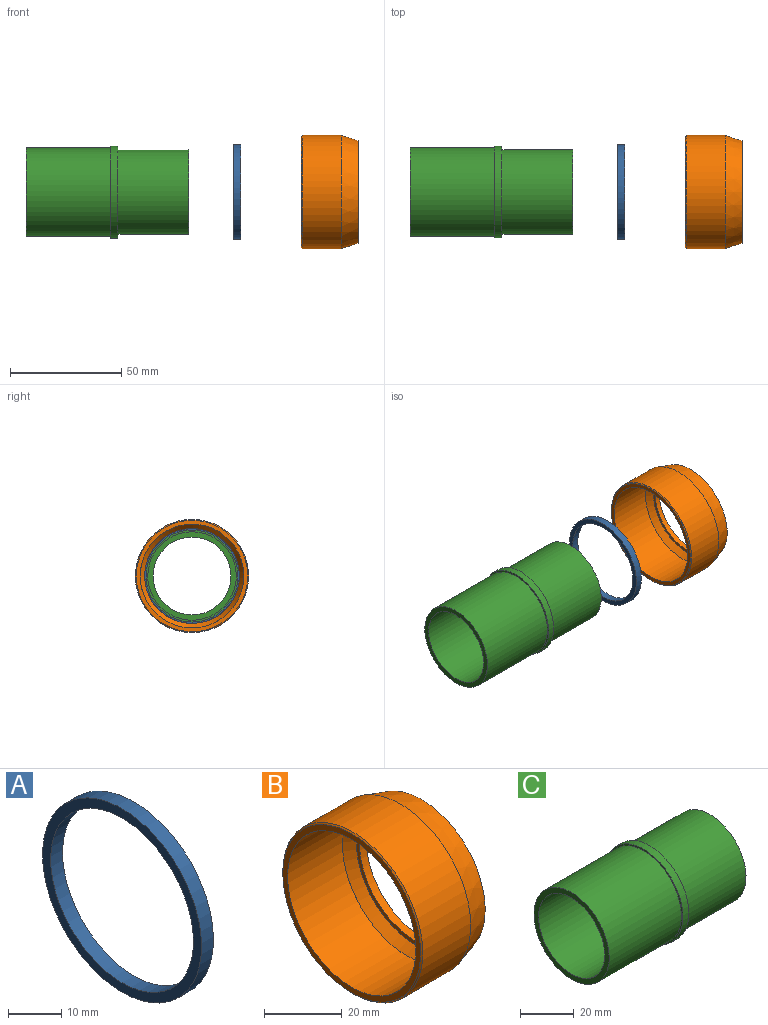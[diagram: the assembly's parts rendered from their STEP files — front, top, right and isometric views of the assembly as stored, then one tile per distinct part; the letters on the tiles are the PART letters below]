
ASSEMBLY  parts=3 mates=2
PART A: 4 faces, bbox 3.2x42.4x42.4 mm
  f0: cylinder r=19.05mm len=38.1mm, axis (-1,0,0), area 380mm2, adj f2,f3
  f1: cylinder r=21.21mm len=42.42mm, axis (-1,0,0), area 423.1mm2, adj f2,f3
  f2: plane 42.42x42.42mm, normal (1,0,0), area 273.1mm2, adj f0,f1
  f3: plane 42.42x42.42mm, normal (-1,0,0), area 273.1mm2, adj f0,f1
PART B: 11 faces, bbox 25.4x50.8x50.8 mm
  f0: cylinder r=20.12mm len=40.23mm, axis (-1,0,0), area 305mm2, adj f2,f5
  f1: cylinder r=25.4mm len=50.8mm, axis (-1,0,0), area 2774.2mm2, adj f9,f10
  f2: plane 46.08x46.08mm, normal (1,0,0), area 396mm2, adj f0,f9
  f3: plane 50.01x50.01mm, normal (-1,0,0), area 263.4mm2, adj f6,f10
  f4: cylinder r=21.27mm len=42.55mm, axis (-1,0,0), area 3.4mm2, adj f5,f8
  f5: plane 42.55x42.55mm, normal (-1,0,0), area 150.3mm2, adj f0,f4
  f6: cylinder r=23.27mm len=46.53mm, axis (-1,0,0), area 2911.1mm2, adj f3,f7
  f7: plane 46.53x46.53mm, normal (-1,0,0), area 1.9mm2, adj f6,f8
  f8: cone r=23.25mm half-angle=33deg, axis (-1,0,0), area 508.5mm2, adj f4,f7
  f9: cone r=23.04mm half-angle=17.2deg, axis (-1,0,0), area 1214mm2, adj f1,f2
  f10: cone r=25.4mm half-angle=45deg, axis (1,0,0), area 88.9mm2, adj f1,f3
PART C: 8 faces, bbox 73x41.3x41.3 mm
  f0: cylinder r=20.64mm len=41.28mm, axis (-1,0,0), area 411.7mm2, adj f4,f7
  f1: plane 38.1x38.1mm, normal (1,0,0), area 182.1mm2, adj f3,f6
  f2: plane 39.69x39.69mm, normal (-1,0,0), area 279.1mm2, adj f3,f5
  f3: cylinder r=17.46mm len=73.03mm, axis (-1,0,0), area 8012.3mm2, adj f1,f2
  f4: plane 41.28x41.28mm, normal (-1,0,0), area 100.9mm2, adj f0,f5
  f5: cylinder r=19.84mm len=39.69mm, axis (-1,0,0), area 4750.4mm2, adj f2,f4
  f6: cylinder r=19.05mm len=38.1mm, axis (1,0,0), area 3800.3mm2, adj f1,f7
  f7: plane 41.28x41.28mm, normal (1,0,0), area 197.9mm2, adj f0,f6
PLACE A rot(axis=(0,0.7,0.72),180deg) t=(96.31,0,0)mm
PLACE B rot(axis=(1,0,0),152.4deg) t=(123.58,0,0)mm
PLACE C at identity fixed
MATE cylindrical A.f0 <-> C.f0  axis (-1,0,0) through (93.14,0,0)mm
MATE cylindrical B.f0 <-> A.f1  axis (-1,0,0) through (146.57,0,0)mm
